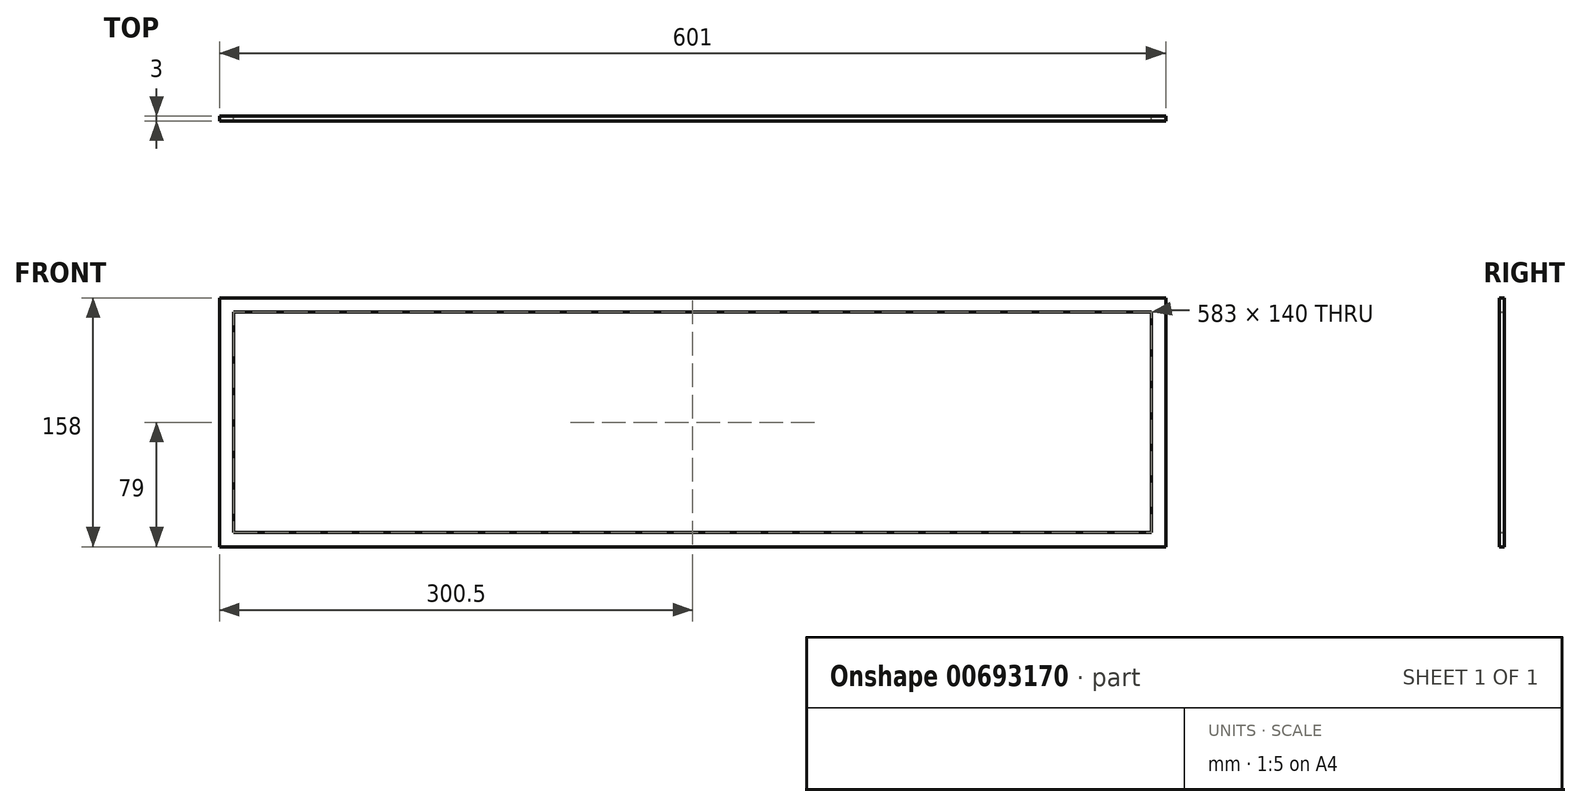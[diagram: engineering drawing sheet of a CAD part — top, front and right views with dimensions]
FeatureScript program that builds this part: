
annotation { "Feature Type Name" : "Feature", "Feature Type Description" : "" }
export const myFeature = defineFeature(function(context is Context, id is Id, definition is map)
    precondition{}
    {
        {
            var Q0;
            Q0=qCreatedBy(makeId("Front.planeOp"),FACE);
            var sketch = newSketch(context, id + "F0", { "sketchPlane" : qUnion([Q0])});
            skLineSegment(sketch, "E0.bottom", {"start": v(-301.5, 80) * mm, "end": v(301.5, 80) * mm});
            skLineSegment(sketch, "E0.top", {"start": v(-301.5, -80) * mm, "end": v(301.5, -80) * mm});
            skLineSegment(sketch, "E0.left", {"start": v(-301.5, 80) * mm, "end": v(-301.5, -80) * mm});
            skLineSegment(sketch, "E0.right", {"start": v(301.5, 80) * mm, "end": v(301.5, -80) * mm});
            skPoint(sketch, "E0.middle", {"position": v(0, 0) * mm});
            skLineSegment(sketch, "E1.0", {"start": v(-291.5, 70) * mm, "end": v(291.5, 70) * mm});
            skLineSegment(sketch, "E1.1", {"start": v(-291.5, 70) * mm, "end": v(-291.5, -70) * mm});
            skLineSegment(sketch, "E1.2", {"start": v(-291.5, -70) * mm, "end": v(291.5, -70) * mm});
            skLineSegment(sketch, "E1.3", {"start": v(291.5, 70) * mm, "end": v(291.5, -70) * mm});
            skSolve(sketch);
        }
        {
            var Q0;
            Q0 = qSketchRegion(id + "F0", true);
            extrude(context, id + "F1", {"entities" : qUnion([Q0]), "depth" : 3 * mm, "offsetDistance" : 25 * mm});
        }
        {
            var Q0;
            Q0=makeQuery(id+"F1.opExtrude","CAP_FACE",FACE,{"disambiguationData":[OSD([sQuery(id+"F0.wireOp",EDGE,"E0.bottom"),sQuery(id+"F0.wireOp",EDGE,"E0.top"),sQuery(id+"F0.wireOp",EDGE,"E0.left"),sQuery(id+"F0.wireOp",EDGE,"E0.right"),sQuery(id+"F0.wireOp",EDGE,"E1.0"),sQuery(id+"F0.wireOp",EDGE,"E1.1"),sQuery(id+"F0.wireOp",EDGE,"E1.2"),sQuery(id+"F0.wireOp",EDGE,"E1.3")])],"isStart":false});
            var sketch = newSketch(context, id + "F2", { "sketchPlane" : qUnion([Q0])});
            skLineSegment(sketch, "E2.0.0", {"start": v(301.5, 80) * mm, "end": v(-301.5, 80) * mm});
            skLineSegment(sketch, "E2.0.1", {"start": v(-301.5, 80) * mm, "end": v(-301.5, -80) * mm});
            skLineSegment(sketch, "E2.0.2", {"start": v(-301.5, -80) * mm, "end": v(301.5, -80) * mm});
            skLineSegment(sketch, "E2.0.3", {"start": v(301.5, -80) * mm, "end": v(301.5, 80) * mm});
            skLineSegment(sketch, "E3.0", {"start": v(300.5, 79) * mm, "end": v(-300.5, 79) * mm});
            skLineSegment(sketch, "E3.1", {"start": v(300.5, -79) * mm, "end": v(300.5, 79) * mm});
            skLineSegment(sketch, "E3.2", {"start": v(-300.5, -79) * mm, "end": v(300.5, -79) * mm});
            skLineSegment(sketch, "E3.3", {"start": v(-300.5, 79) * mm, "end": v(-300.5, -79) * mm});
            skSolve(sketch);
        }
        {
            var Q0;
            Q0 = qSketchRegion(id + "F2", true);
            extrude(context, id + "F3", {"entities" : qUnion([Q0]), "operationType" : NewBodyOperationType.REMOVE, "oppositeDirection" : true, "depth" : 25 * mm, "offsetDistance" : 25 * mm});
        }
    });
